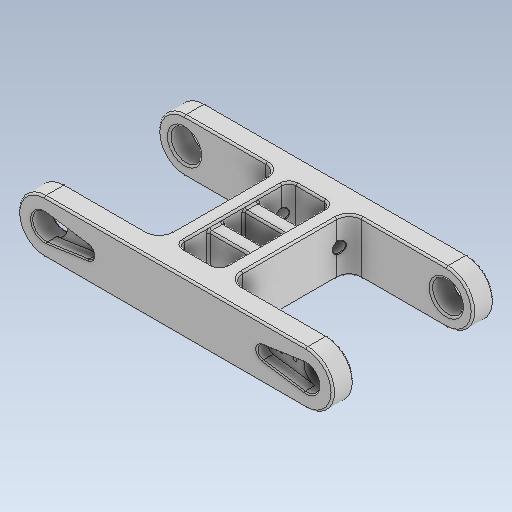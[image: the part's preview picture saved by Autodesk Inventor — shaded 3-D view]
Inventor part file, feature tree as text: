
AUTODESK INVENTOR PART (.ipt)
format: ipt  version: 2020.3 (Build 243373000, 373)  size: 429,568 bytes
history: native  units: mm
features: sketch x7, other x3
ambient origin geometry x8: Origin, YZ Plane, XZ Plane, XY Plane, X Axis, Y Axis, Z Axis, Center Point
bodies: Solid1 (feature_tree)
feature tree (10):
  other  "LegMiddle_Final_1.ipt"
  other  "Solid1::LegMiddle_Final_1.ipt"
  other  "TaggingFeature1"
  sketch  "Sketch1"  dims[d0=10.0mm]
  sketch  "Sketch2"
  sketch  "Sketch5"
  sketch  "Sketch14"
  sketch  "Sketch6"
  sketch  "Sketch12"
  sketch  "Sketch13"
